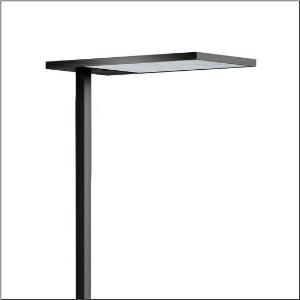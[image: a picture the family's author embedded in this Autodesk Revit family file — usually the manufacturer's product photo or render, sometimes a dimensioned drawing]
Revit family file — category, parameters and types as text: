
# Revit family: silica_r__21_floor_r_51mx53sg4db_4ec3
name_source: partatom
category: Lighting Fixtures
units: mm (PartAtom-declared; Revit-internal decimal feet)

## family parameters
Cut with Voids When Loaded = No
Host = Face
Light Source = No
Part Type = Normal
Room Calculation Point = No
Round Connector Dimension = Use Diameter
Shared = No

## types (1)
- Silica® 21 Floor R (1 x LED, 15000 lm, 106.4 W, 4000K)
    Apparent Load = 106 VA
    CIE Flux Codes = 54 86 97 13 100
    Color Rendering = 80
    Color Temperature = 4000K
    Default Elevation = 1800 mm
    Description = Silica® 21 Floor R, floorstanding luminaire, of PMMA, primary optical cover: prismatic diffuser, of PMMA, CAT 2 (L<= 3000cd/m²), light emission: indirect/direct distribution, primary light characteristic: symmetric, installation type: not mounted, LED, rated luminous flux: 15.000lm, luminous efficacy: 141lm/W, light colour: 840, colour temperature: 4000K, control gear: ECG DALI, daylight-dependent control, mains connection: 230V, 50Hz, connection cable pre-assembled, cable length: 2,5m, rated input power: 106.4W, luminaire head, of aluminium, jet black (RAL 9005), length: 650mm, width: 350mm, supporting column, angular, of aluminium, jet black (RAL 9005), baseplate, of steel, jet black (RAL 9005), protection rating (complete): IP20, insulation class (complete): insulation class I (protective earthing), certification: CE, standard: EN 50419, packaging unit: 1 piece
    Height = 18 mm
    Lamp = 1 x LED
    Lamp Light Flux = 15000 lm
    Lamp Power = 106.4 W
    Lamp count = 1
    Length = 650 mm
    Luminous efficacy = 141 lm/W
    Manufacturer = Siteco
    ModVariant = No
    Model = 51MX53SG4DB
    Mounting Place = Floor
    Mounting Type = Freestanding
    Number of Poles = 1
    OnlyDefault = Yes
    Power Factor = 1
    Product Name = Silica® 21 Floor R
    Product group = floorstanding luminaire
    ProductGroupID = 1302
    Protection Class = Protection class I
    Protection Degree = IP 20
    RLX_Detail_Level = 1
    RlxData = <blob elided: 21937 chars, md5=c71159c6>
    Socket = socket
    Standby Power = 0 W
    System Light Flux = 15000 lm
    System Power = 106 W
    Type Comments = Product without accessories
    Type Image = l_1007011.jpg
    URL = http://relux.com
    VarID = ---
    Voltage = 0 V
    Weight = 0.00 kg
    Width = 350 mm

## geometry (parser evidence)
native form markers: Blend x4, Sweep x12
no freeform markers — native parametric forms only
